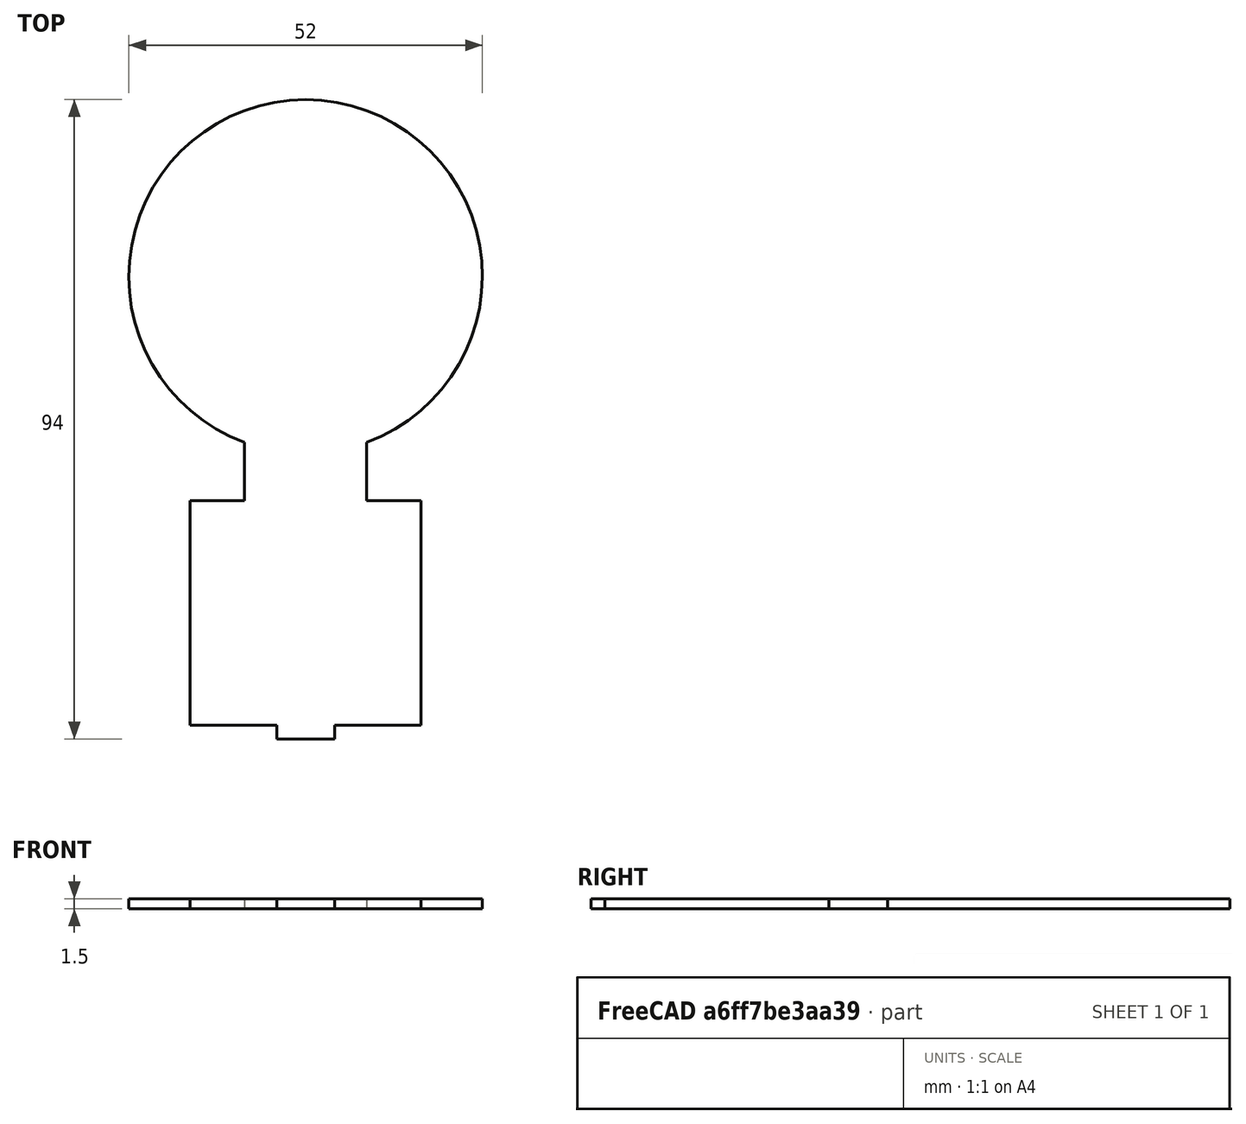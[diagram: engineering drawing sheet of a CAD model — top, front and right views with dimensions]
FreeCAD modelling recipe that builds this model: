
FCSTD DOCUMENT  (FreeCAD 0.14R3702 (Git))
Label: Plate
License: CC-BY 3.0
LicenseURL: http://creativecommons.org/licenses/by/3.0/
objects: Sketcher::SketchObject×1, PartDesign::Pad×1
note: 3 computed .brp shape members not serialized (recipe doc carries the construction recipe); baked Part::Feature solids carry a one-line shape summary decoded from their .brp

FEATURE [Sketcher::SketchObject] Sketch
  Placement = pos=(0,0,0) rot=(1,0,0;3.14159rad)
  sketch-geometry (12):
    g0: LineSegment StartX=9 StartY=30 StartZ=0 EndX=9 EndY=21.3926 EndZ=0
    g1: LineSegment StartX=-9 StartY=21.3926 StartZ=0 EndX=-9 EndY=30 EndZ=0
    g2: ArcOfCircle CenterX=0 CenterY=-3 CenterZ=0 NormalX=0 NormalY=0 NormalZ=1 Radius=26 StartAngle=1.92426 EndAngle=7.50051
    g3: LineSegment StartX=-4.26122 StartY=65 StartZ=0 EndX=4.26122 EndY=65 EndZ=0
    g4: LineSegment StartX=4.26122 StartY=65 StartZ=0 EndX=4.26122 EndY=63 EndZ=0
    g5: LineSegment StartX=-4.26122 StartY=63 StartZ=0 EndX=-4.26122 EndY=65 EndZ=0
    g6: LineSegment StartX=-4.26122 StartY=63 StartZ=0 EndX=-17 EndY=63 EndZ=0
    g7: LineSegment StartX=-17 StartY=63 StartZ=0 EndX=-17 EndY=30 EndZ=0
    g8: LineSegment StartX=-17 StartY=30 StartZ=0 EndX=-9 EndY=30 EndZ=0
    g9: LineSegment StartX=9 StartY=30 StartZ=0 EndX=17 EndY=30 EndZ=0
    g10: LineSegment StartX=17 StartY=30 StartZ=0 EndX=17 EndY=63 EndZ=0
    g11: LineSegment StartX=17 StartY=63 StartZ=0 EndX=4.26122 EndY=63 EndZ=0
  constraints (35):
    c: Vertical(g0)
    c: Vertical(g1)
    c: Coincident(g2,g0)
    c: DistanceY(g2,g-3) = 68
    c: Radius(g2) = 26
    c: PointOnObject(g2,g-2)
    c: DistanceX(g1,g0) = 18
    c: Coincident(g2,g1)
    c: Coincident(g3,g4)
    c: Coincident(g5,g3)
    c: Horizontal(g3)
    c: Vertical(g4)
    c: Vertical(g5)
    c: Symmetric(g5,g4,g-2)
    c: DistanceY(g3,g-3) = 0
    c: DistanceY(g3,g4) = -2
    c: Equal(g4,g5)
    c: Coincident(g5,g6)
    c: Horizontal(g6)
    c: Coincident(g6,g7)
    c: Vertical(g7)
    c: Coincident(g7,g8)
    c: Horizontal(g8)
    c: Coincident(g0,g9)
    c: Horizontal(g9)
    c: Coincident(g9,g10)
    c: Vertical(g10)
    c: Coincident(g10,g11)
    c: Coincident(g11,g4)
    c: Horizontal(g11)
    c: Equal(g7,g10)
    c: DistanceY(g10,g9) = -33
    c: Equal(g11,g6)
    c: DistanceX(g7,g9) = 34
    c: Coincident(g1,g8)
FEATURE [PartDesign::Pad] Pad
  Length = 1.5
  Length2 = 100
  Placement = pos=(0,0,0) rot=(1,0,0;3.14159rad)
  Sketch = -> Sketch
  Type = 0
